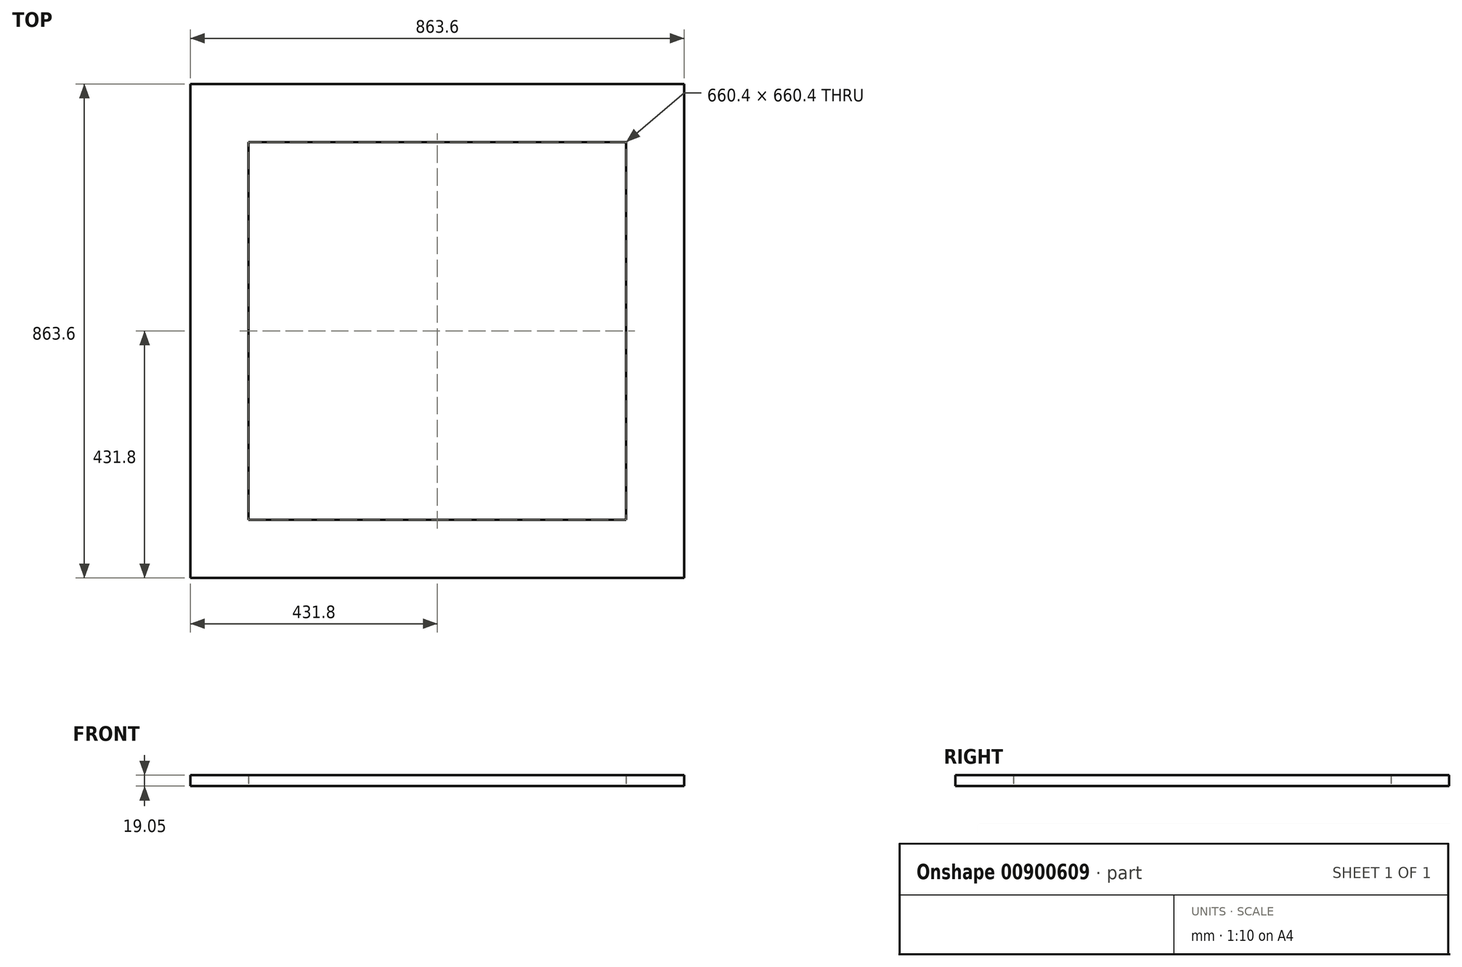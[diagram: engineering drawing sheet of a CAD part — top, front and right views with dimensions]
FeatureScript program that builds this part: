
annotation { "Feature Type Name" : "Feature", "Feature Type Description" : "" }
export const myFeature = defineFeature(function(context is Context, id is Id, definition is map)
    precondition{}
    {
        {
            var Q0;
            Q0=qCreatedBy(makeId("Top.planeOp"),FACE);
            var sketch = newSketch(context, id + "F0", { "sketchPlane" : qUnion([Q0])});
            skLineSegment(sketch, "E0.bottom", {"start": v(431.8, 431.8) * mm, "end": v(-431.8, 431.8) * mm});
            skLineSegment(sketch, "E0.top", {"start": v(431.8, -431.8) * mm, "end": v(-431.8, -431.8) * mm});
            skLineSegment(sketch, "E0.left", {"start": v(431.8, 431.8) * mm, "end": v(431.8, -431.8) * mm});
            skLineSegment(sketch, "E0.right", {"start": v(-431.8, 431.8) * mm, "end": v(-431.8, -431.8) * mm});
            skPoint(sketch, "E0.middle", {"position": v(0, 0) * mm});
            skLineSegment(sketch, "E1.bottom", {"start": v(330.2, 330.2) * mm, "end": v(-330.2, 330.2) * mm});
            skLineSegment(sketch, "E1.top", {"start": v(330.2, -330.2) * mm, "end": v(-330.2, -330.2) * mm});
            skLineSegment(sketch, "E1.left", {"start": v(330.2, 330.2) * mm, "end": v(330.2, -330.2) * mm});
            skLineSegment(sketch, "E1.right", {"start": v(-330.2, 330.2) * mm, "end": v(-330.2, -330.2) * mm});
            skSolve(sketch);
        }
        {
            var Q0;
            Q0=makeQuery(id+"F0.imprint","IMPRINT",FACE,{"disambiguationData":[TD([[makeQuery(id+"F0.imprint","IMPRINT",EDGE,{"derivedFrom":sQuery(id+"F0.wireOp",EDGE,"E0.bottom")}),1.0]])]});
            extrude(context, id + "F1", {"entities" : qUnion([Q0]), "depth" : 19.05 * mm, "offsetDistance" : 25.4 * mm});
        }
    });
